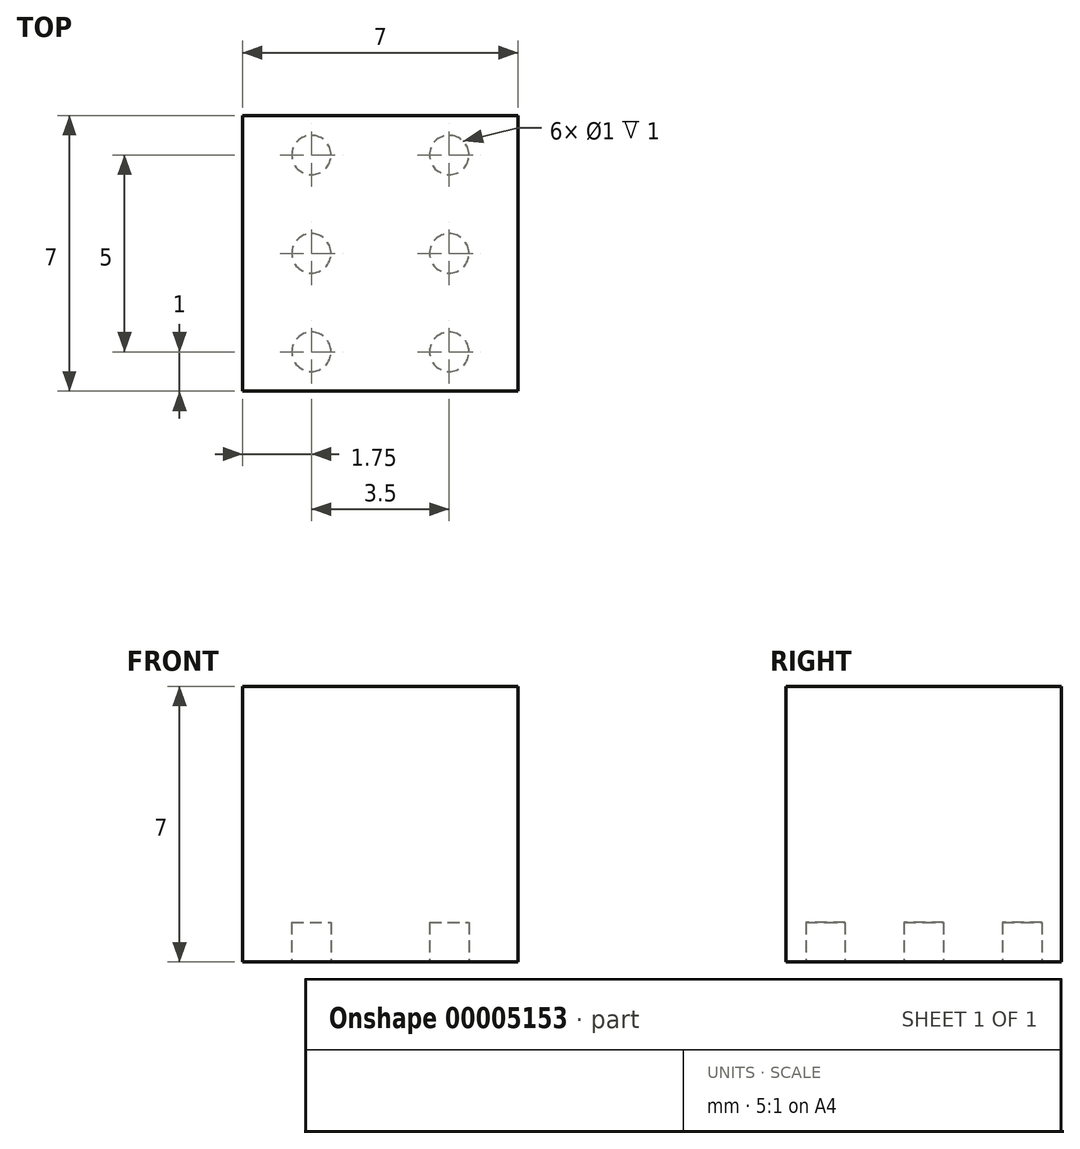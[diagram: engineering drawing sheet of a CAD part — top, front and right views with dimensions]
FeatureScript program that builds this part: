
annotation { "Feature Type Name" : "Feature", "Feature Type Description" : "" }
export const myFeature = defineFeature(function(context is Context, id is Id, definition is map)
    precondition{}
    {
        {
            var Q0;
            Q0=qCreatedBy(makeId("Front.planeOp"),FACE);
            var sketch = newSketch(context, id + "F0", { "sketchPlane" : qUnion([Q0])});
            skLineSegment(sketch, "E0.rect.bottom", {"start": v(3.5, -3.5) * mm, "end": v(-3.5, -3.5) * mm});
            skLineSegment(sketch, "E0.rect.top", {"start": v(3.5, 3.5) * mm, "end": v(-3.5, 3.5) * mm});
            skLineSegment(sketch, "E0.rect.left", {"start": v(3.5, -3.5) * mm, "end": v(3.5, 3.5) * mm});
            skLineSegment(sketch, "E0.rect.right", {"start": v(-3.5, -3.5) * mm, "end": v(-3.5, 3.5) * mm});
            skPoint(sketch, "E0.rect.middle", {"position": v(0, 0) * mm});
            skSolve(sketch);
        }
        {
            var Q0;
            Q0 = qSketchRegion(id + "F0", true);
            extrude(context, id + "F1", {"entities" : qUnion([Q0]), "depth" : 7 * mm});
        }
        {
            var Q0;
            Q0=makeQuery(id+"F1.opExtrude","SWEPT_FACE",FACE,{"disambiguationData":[OSD([sQuery(id+"F0.wireOp",EDGE,"E0.rect.bottom")])]});
            var sketch = newSketch(context, id + "F2", { "sketchPlane" : qUnion([Q0])});
            skCircle(sketch, "E1", {"center": v(-1.75, 6) * mm, "radius": 0.5 * mm});
            skCircle(sketch, "E2", {"center": v(-1.75, 3.5) * mm, "radius": 0.5 * mm});
            skCircle(sketch, "E3", {"center": v(-1.75, 1) * mm, "radius": 0.5 * mm});
            skCircle(sketch, "E4", {"center": v(1.75, 6) * mm, "radius": 0.5 * mm});
            skCircle(sketch, "E5", {"center": v(1.75, 3.5) * mm, "radius": 0.5 * mm});
            skCircle(sketch, "E6", {"center": v(1.75, 1) * mm, "radius": 0.5 * mm});
            skSolve(sketch);
        }
        {
            var Q0;
            Q0=makeQuery(id+"F2.imprint","IMPRINT",FACE,{"disambiguationData":[TD([[makeQuery(id+"F2.imprint","IMPRINT",EDGE,{"derivedFrom":sQuery(id+"F2.wireOp",EDGE,"E1")}),1.0]])]});
            var Q1;
            Q1=makeQuery(id+"F2.imprint","IMPRINT",FACE,{"disambiguationData":[TD([[makeQuery(id+"F2.imprint","IMPRINT",EDGE,{"derivedFrom":sQuery(id+"F2.wireOp",EDGE,"E4")}),1.0]])]});
            var Q2;
            Q2=makeQuery(id+"F2.imprint","IMPRINT",FACE,{"disambiguationData":[TD([[makeQuery(id+"F2.imprint","IMPRINT",EDGE,{"derivedFrom":sQuery(id+"F2.wireOp",EDGE,"E2")}),1.0]])]});
            var Q3;
            Q3=makeQuery(id+"F2.imprint","IMPRINT",FACE,{"disambiguationData":[TD([[makeQuery(id+"F2.imprint","IMPRINT",EDGE,{"derivedFrom":sQuery(id+"F2.wireOp",EDGE,"E5")}),1.0]])]});
            var Q4;
            Q4=makeQuery(id+"F2.imprint","IMPRINT",FACE,{"disambiguationData":[TD([[makeQuery(id+"F2.imprint","IMPRINT",EDGE,{"derivedFrom":sQuery(id+"F2.wireOp",EDGE,"E3")}),1.0]])]});
            var Q5;
            Q5=makeQuery(id+"F2.imprint","IMPRINT",FACE,{"disambiguationData":[TD([[makeQuery(id+"F2.imprint","IMPRINT",EDGE,{"derivedFrom":sQuery(id+"F2.wireOp",EDGE,"E6")}),1.0]])]});
            extrude(context, id + "F3", {"entities" : qUnion([Q0, Q1, Q2, Q3, Q4, Q5]), "operationType" : NewBodyOperationType.REMOVE, "oppositeDirection" : true, "depth" : 1 * mm});
        }
    });
